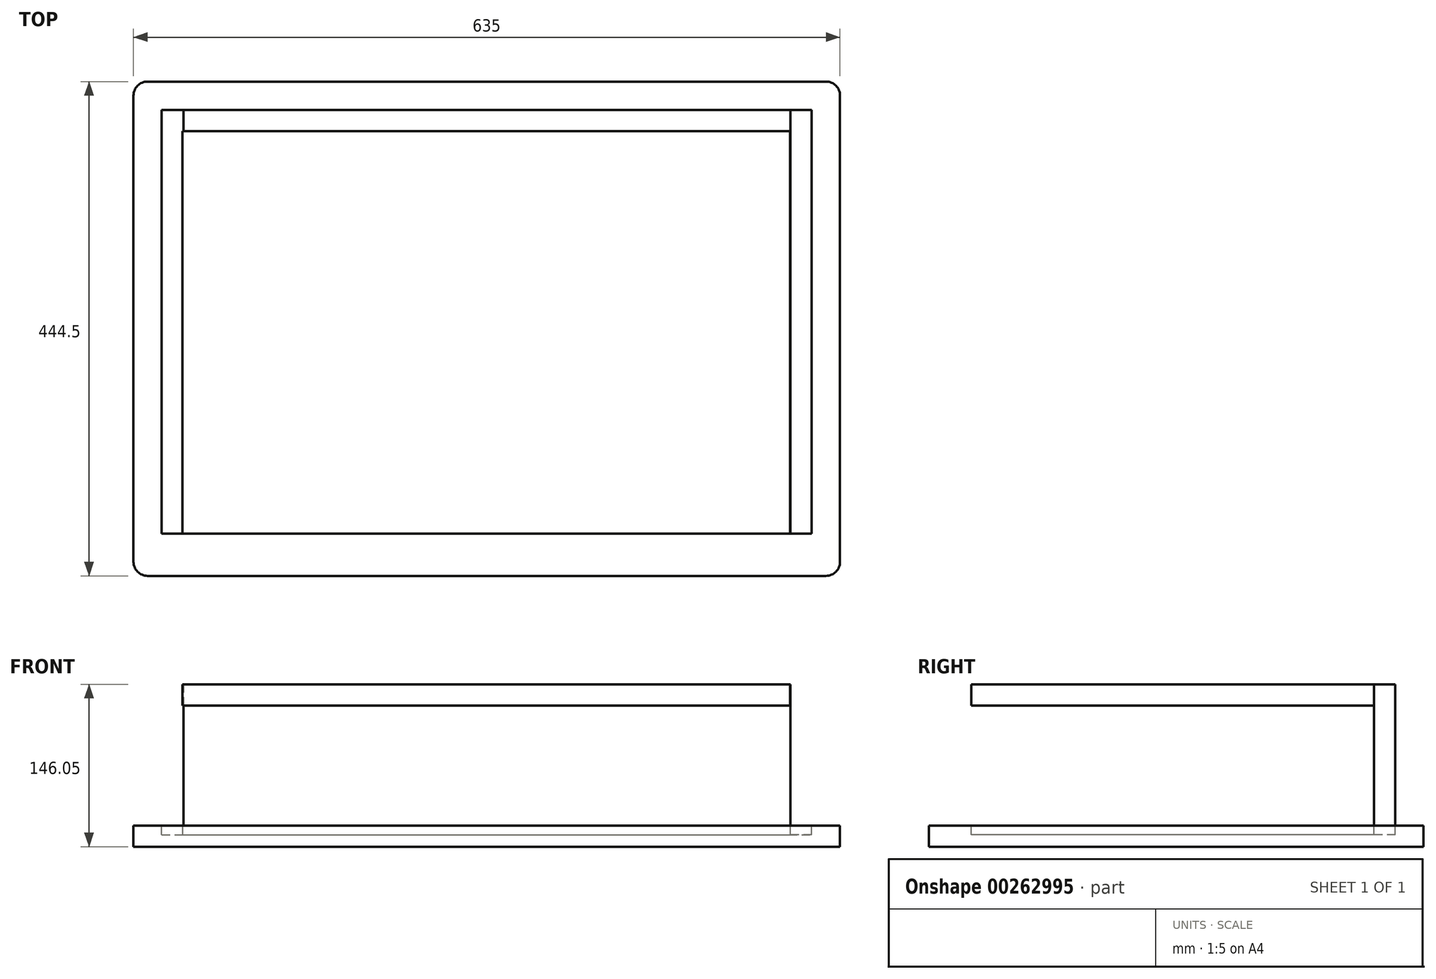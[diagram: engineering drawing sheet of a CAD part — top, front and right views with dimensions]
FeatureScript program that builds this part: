
annotation { "Feature Type Name" : "Feature", "Feature Type Description" : "" }
export const myFeature = defineFeature(function(context is Context, id is Id, definition is map)
    precondition{}
    {
        {
            var Q0;
            Q0=qCreatedBy(makeId("Top.planeOp"),FACE);
            var sketch = newSketch(context, id + "F0", { "sketchPlane" : qUnion([Q0])});
            skLineSegment(sketch, "E0.bottom", {"start": v(-304.8, 222.25) * mm, "end": v(304.8, 222.25) * mm});
            skLineSegment(sketch, "E0.top", {"start": v(-304.8, -222.25) * mm, "end": v(304.8, -222.25) * mm});
            skLineSegment(sketch, "E0.left", {"start": v(-317.5, 209.55) * mm, "end": v(-317.5, -209.55) * mm});
            skLineSegment(sketch, "E0.right", {"start": v(317.5, 209.55) * mm, "end": v(317.5, -209.55) * mm});
            skPoint(sketch, "E0.middle", {"position": v(0, 0) * mm});
            skPoint(sketch, "E1.visualSharp", {"position": v(-317.5, 222.25) * mm});
            skArc(sketch, "E1.filletArc", {"start": v(-304.8, 222.25) * mm, "mid": v(-313.78, 218.53) * mm, "end": v(-317.5, 209.55) * mm});
            skPoint(sketch, "E2.visualSharp", {"position": v(317.5, 222.25) * mm});
            skArc(sketch, "E2.filletArc", {"start": v(317.5, 209.55) * mm, "mid": v(313.78, 218.53) * mm, "end": v(304.8, 222.25) * mm});
            skPoint(sketch, "E3.visualSharp", {"position": v(317.5, -222.25) * mm});
            skArc(sketch, "E3.filletArc", {"start": v(304.8, -222.25) * mm, "mid": v(313.78, -218.53) * mm, "end": v(317.5, -209.55) * mm});
            skPoint(sketch, "E4.visualSharp", {"position": v(-317.5, -222.25) * mm});
            skArc(sketch, "E4.filletArc", {"start": v(-317.5, -209.55) * mm, "mid": v(-313.78, -218.53) * mm, "end": v(-304.8, -222.25) * mm});
            skSolve(sketch);
        }
        {
            var Q0;
            Q0 = qSketchRegion(id + "F0", true);
            extrude(context, id + "F1", {"entities" : qUnion([Q0]), "depth" : 19.05 * mm});
        }
        {
            var Q0;
            Q0=makeQuery(id+"F1.opExtrude","CAP_FACE",FACE,{"disambiguationData":[OSD([sQuery(id+"F0.wireOp",EDGE,"E0.bottom"),sQuery(id+"F0.wireOp",EDGE,"E0.top"),sQuery(id+"F0.wireOp",EDGE,"E0.left"),sQuery(id+"F0.wireOp",EDGE,"E0.right"),sQuery(id+"F0.wireOp",EDGE,"E1.filletArc"),sQuery(id+"F0.wireOp",EDGE,"E2.filletArc"),sQuery(id+"F0.wireOp",EDGE,"E3.filletArc"),sQuery(id+"F0.wireOp",EDGE,"E4.filletArc")])],"isStart":false});
            var sketch = newSketch(context, id + "F2", { "sketchPlane" : qUnion([Q0])});
            skLineSegment(sketch, "E5.bottom", {"start": v(-292.1, 196.85) * mm, "end": v(292.1, 196.85) * mm});
            skLineSegment(sketch, "E5.top", {"start": v(-292.1, 177.8) * mm, "end": v(292.1, 177.8) * mm});
            skLineSegment(sketch, "E5.left", {"start": v(-292.1, 196.85) * mm, "end": v(-292.1, 177.8) * mm});
            skLineSegment(sketch, "E5.right", {"start": v(292.1, 196.85) * mm, "end": v(292.1, 177.8) * mm});
            skPoint(sketch, "E5.middle", {"position": v(0, 187.33) * mm});
            skSolve(sketch);
        }
        {
            var Q0;
            Q0 = qSketchRegion(id + "F2", true);
            extrude(context, id + "F3", {"entities" : qUnion([Q0]), "operationType" : NewBodyOperationType.REMOVE, "oppositeDirection" : true, "depth" : 8.38 * mm});
        }
        {
            var Q0;
            Q0=makeQuery(id+"F1.opExtrude","CAP_FACE",FACE,{"disambiguationData":[OSD([sQuery(id+"F0.wireOp",EDGE,"E0.bottom"),sQuery(id+"F0.wireOp",EDGE,"E0.top"),sQuery(id+"F0.wireOp",EDGE,"E0.left"),sQuery(id+"F0.wireOp",EDGE,"E0.right"),sQuery(id+"F0.wireOp",EDGE,"E1.filletArc"),sQuery(id+"F0.wireOp",EDGE,"E2.filletArc"),sQuery(id+"F0.wireOp",EDGE,"E3.filletArc"),sQuery(id+"F0.wireOp",EDGE,"E4.filletArc")])],"isStart":false});
            var sketch = newSketch(context, id + "F4", { "sketchPlane" : qUnion([Q0])});
            skLineSegment(sketch, "E6.bottom", {"start": v(-292.1, 177.8) * mm, "end": v(-273.05, 177.8) * mm});
            skLineSegment(sketch, "E6.top", {"start": v(-292.1, -184.15) * mm, "end": v(-273.05, -184.15) * mm});
            skLineSegment(sketch, "E6.left", {"start": v(-292.1, 177.8) * mm, "end": v(-292.1, -184.15) * mm});
            skLineSegment(sketch, "E6.right", {"start": v(-273.05, 177.8) * mm, "end": v(-273.05, -184.15) * mm});
            skSolve(sketch);
        }
        {
            var Q0;
            Q0 = qSketchRegion(id + "F4", true);
            extrude(context, id + "F5", {"entities" : qUnion([Q0]), "operationType" : NewBodyOperationType.REMOVE, "oppositeDirection" : true, "depth" : 8.38 * mm});
        }
        {
            var Q0;
            Q0=makeQuery(id+"F1.opExtrude","CAP_FACE",FACE,{"disambiguationData":[OSD([sQuery(id+"F0.wireOp",EDGE,"E0.bottom"),sQuery(id+"F0.wireOp",EDGE,"E0.top"),sQuery(id+"F0.wireOp",EDGE,"E0.left"),sQuery(id+"F0.wireOp",EDGE,"E0.right"),sQuery(id+"F0.wireOp",EDGE,"E1.filletArc"),sQuery(id+"F0.wireOp",EDGE,"E2.filletArc"),sQuery(id+"F0.wireOp",EDGE,"E3.filletArc"),sQuery(id+"F0.wireOp",EDGE,"E4.filletArc")])],"isStart":false});
            var sketch = newSketch(context, id + "F6", { "sketchPlane" : qUnion([Q0])});
            skLineSegment(sketch, "E7.bottom", {"start": v(292.1, 177.8) * mm, "end": v(273.05, 177.8) * mm});
            skLineSegment(sketch, "E7.top", {"start": v(292.1, -184.15) * mm, "end": v(273.05, -184.15) * mm});
            skLineSegment(sketch, "E7.left", {"start": v(292.1, 177.8) * mm, "end": v(292.1, -184.15) * mm});
            skLineSegment(sketch, "E7.right", {"start": v(273.05, 177.8) * mm, "end": v(273.05, -184.15) * mm});
            skSolve(sketch);
        }
        {
            var Q0;
            Q0 = qSketchRegion(id + "F6", true);
            extrude(context, id + "F7", {"entities" : qUnion([Q0]), "operationType" : NewBodyOperationType.REMOVE, "oppositeDirection" : true, "depth" : 8.38 * mm});
        }
        {
            var Q0;
            Q0=makeQuery(id+"F2.imprint","IMPRINT",FACE,{"disambiguationData":[TD([[makeQuery(id+"F2.imprint","IMPRINT",EDGE,{"derivedFrom":sQuery(id+"F2.wireOp",EDGE,"E5.bottom")}),-1.0]])]});
            var sketch = newSketch(context, id + "F8", { "sketchPlane" : qUnion([Q0])});
            skLineSegment(sketch, "E8.bottom", {"start": v(273.05, 177.8) * mm, "end": v(-272.44, 177.8) * mm});
            skLineSegment(sketch, "E8.top", {"start": v(273.05, 196.85) * mm, "end": v(-272.44, 196.85) * mm});
            skLineSegment(sketch, "E8.left", {"start": v(273.05, 177.8) * mm, "end": v(273.05, 196.85) * mm});
            skLineSegment(sketch, "E8.right", {"start": v(-272.44, 177.8) * mm, "end": v(-272.44, 196.85) * mm});
            skSolve(sketch);
        }
        {
            var Q0;
            Q0 = qSketchRegion(id + "F8", true);
            extrude(context, id + "F9", {"entities" : qUnion([Q0]), "depth" : 127 * mm});
        }
        {
            var Q0;
            Q0=makeQuery(id+"F9.opExtrude","CAP_FACE",FACE,{"disambiguationData":[OSD([sQuery(id+"F8.wireOp",EDGE,"E8.bottom"),sQuery(id+"F8.wireOp",EDGE,"E8.top"),sQuery(id+"F8.wireOp",EDGE,"E8.left"),sQuery(id+"F8.wireOp",EDGE,"E8.right")])],"isStart":false});
            var sketch = newSketch(context, id + "F10", { "sketchPlane" : qUnion([Q0])});
            skLineSegment(sketch, "E9.bottom", {"start": v(-273.55, 177.8) * mm, "end": v(272.55, 177.8) * mm});
            skLineSegment(sketch, "E9.top", {"start": v(-273.55, -184.15) * mm, "end": v(272.55, -184.15) * mm});
            skLineSegment(sketch, "E9.left", {"start": v(-273.55, 177.8) * mm, "end": v(-273.55, -184.15) * mm});
            skLineSegment(sketch, "E9.right", {"start": v(272.55, 177.8) * mm, "end": v(272.55, -184.15) * mm});
            skSolve(sketch);
        }
        {
            var Q0;
            Q0 = qSketchRegion(id + "F10", true);
            extrude(context, id + "F11", {"entities" : qUnion([Q0]), "oppositeDirection" : true, "depth" : 19.05 * mm});
        }
    });
